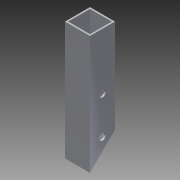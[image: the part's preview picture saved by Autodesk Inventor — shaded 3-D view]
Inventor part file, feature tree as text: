
AUTODESK INVENTOR PART (.ipt)
format: ipt  version: 2013 (Build 170138000, 138)  size: 96,256 bytes
history: native  units: in
note: dims shown in document units (in); Inventor stores cm internally (conversion verified against a paired STEP export)
features: extrude x3, sketch x3, reference x2
ambient origin geometry x8: Origin, YZ Plane, XZ Plane, XY Plane, X Axis, Y Axis, Z Axis, Center Point
bodies: Solid1 (feature_tree)
feature tree (8):
  extrude  "Extrusion1"  Depth=1.0in
  extrude  "Extrusion2"  Depth=4.75in TaperAngle=0.0deg
  extrude  "Extrusion3"  Depth=1.0in TaperAngle=0.0deg
  sketch  "Sketch1"  dims[d0=1.0in d2=1.0in]
  sketch  "Sketch2"  dims[d3=0.0625in d4=4.75in d5=0.0in]
  sketch  "Sketch3"  dims[d6=45.0deg d7=1.0in d8=0.0in d9=1.0in d10=0.0in]
  reference  "Reference1"
  reference  "Reference2"
